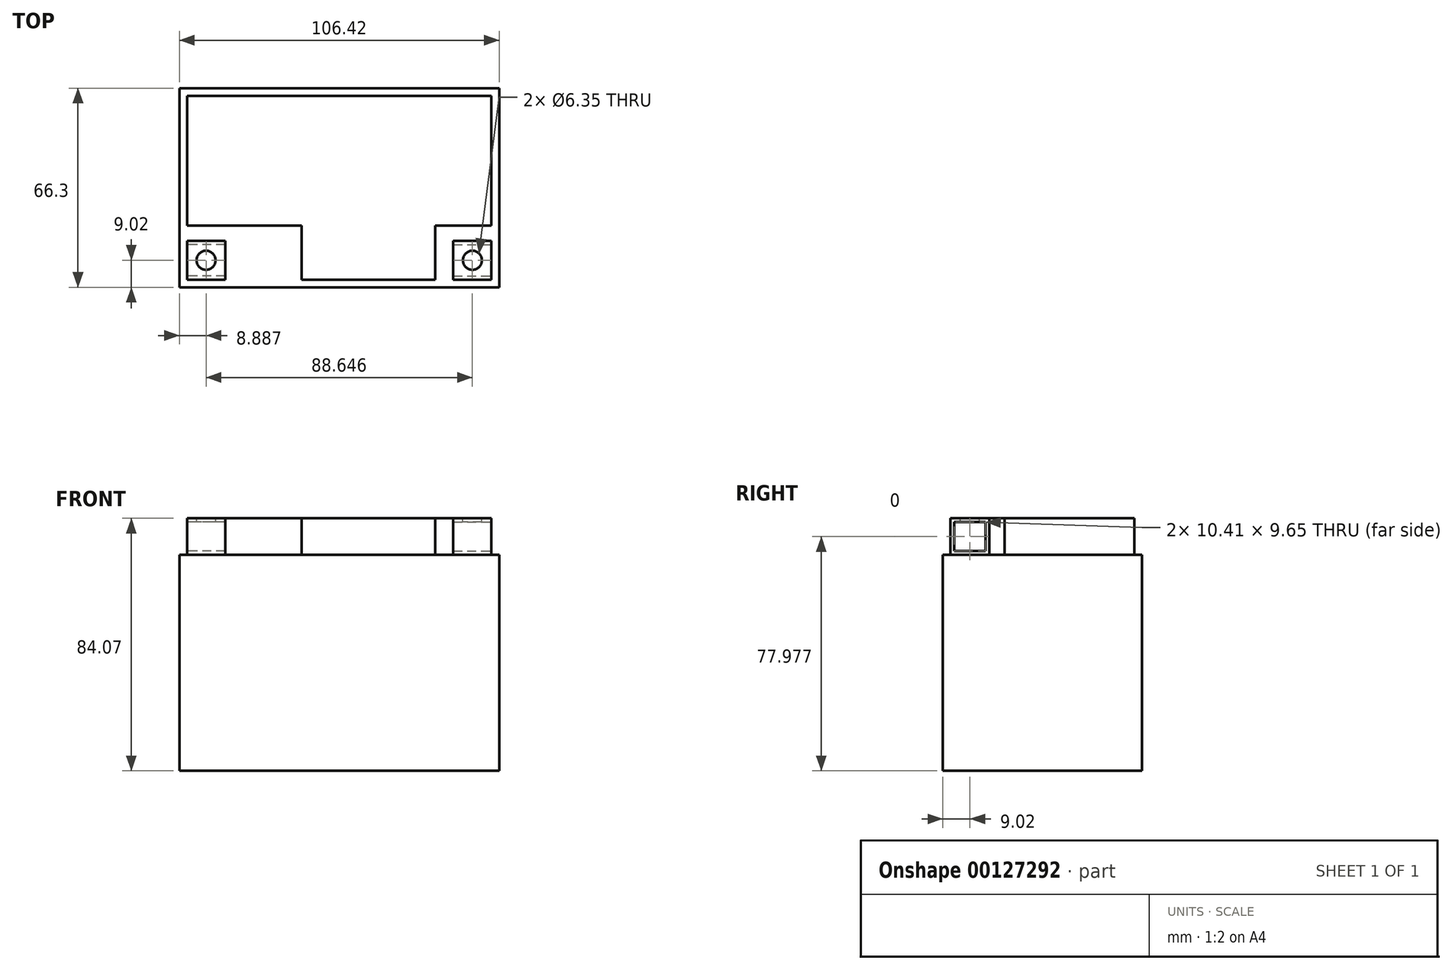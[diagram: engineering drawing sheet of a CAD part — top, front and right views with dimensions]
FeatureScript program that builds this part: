
annotation { "Feature Type Name" : "Feature", "Feature Type Description" : "" }
export const myFeature = defineFeature(function(context is Context, id is Id, definition is map)
    precondition{}
    {
        {
            var Q0;
            Q0=qCreatedBy(makeId("Top.planeOp"),FACE);
            var sketch = newSketch(context, id + "F0", { "sketchPlane" : qUnion([Q0])});
            skLineSegment(sketch, "E0.bottom", {"start": v(53.21, 33.15) * mm, "end": v(-53.21, 33.15) * mm});
            skLineSegment(sketch, "E0.top", {"start": v(53.21, -33.15) * mm, "end": v(-53.21, -33.15) * mm});
            skLineSegment(sketch, "E0.left", {"start": v(53.21, 33.15) * mm, "end": v(53.21, -33.15) * mm});
            skLineSegment(sketch, "E0.right", {"start": v(-53.21, 33.15) * mm, "end": v(-53.21, -33.15) * mm});
            skPoint(sketch, "E0.middle", {"position": v(0, 0) * mm});
            skSolve(sketch);
        }
        {
            var Q0;
            Q0 = qSketchRegion(id + "F0", true);
            extrude(context, id + "F1", {"entities" : qUnion([Q0]), "endBound" : BoundingType.SYMMETRIC, "depth" : 71.88 * mm});
        }
        {
            var Q0;
            Q0=makeQuery(id+"F1.opExtrude","CAP_FACE",FACE,{"disambiguationData":[OSD([sQuery(id+"F0.wireOp",EDGE,"E0.bottom"),sQuery(id+"F0.wireOp",EDGE,"E0.top"),sQuery(id+"F0.wireOp",EDGE,"E0.left"),sQuery(id+"F0.wireOp",EDGE,"E0.right")])],"isStart":false});
            var sketch = newSketch(context, id + "F2", { "sketchPlane" : qUnion([Q0])});
            skLineSegment(sketch, "E1.bottom", {"start": v(-50.67, 30.6) * mm, "end": v(50.67, 30.6) * mm});
            skLineSegment(sketch, "E1.left", {"start": v(-50.67, 30.6) * mm, "end": v(-50.67, -12.57) * mm});
            skLineSegment(sketch, "E1.right", {"start": v(50.67, 30.6) * mm, "end": v(50.67, -12.57) * mm});
            skLineSegment(sketch, "E2.bottom", {"start": v(-50.67, -17.65) * mm, "end": v(-37.97, -17.65) * mm});
            skLineSegment(sketch, "E2.top", {"start": v(-50.67, -30.6) * mm, "end": v(-37.97, -30.6) * mm});
            skLineSegment(sketch, "E2.left", {"start": v(-50.67, -17.65) * mm, "end": v(-50.67, -30.6) * mm});
            skLineSegment(sketch, "E2.right", {"start": v(-37.97, -17.65) * mm, "end": v(-37.97, -30.6) * mm});
            skLineSegment(sketch, "E3.bottom", {"start": v(37.97, -17.65) * mm, "end": v(50.67, -17.65) * mm});
            skLineSegment(sketch, "E3.top", {"start": v(37.97, -30.6) * mm, "end": v(50.67, -30.6) * mm});
            skLineSegment(sketch, "E3.left", {"start": v(37.97, -17.65) * mm, "end": v(37.97, -30.6) * mm});
            skLineSegment(sketch, "E3.right", {"start": v(50.67, -17.65) * mm, "end": v(50.67, -30.6) * mm});
            skLineSegment(sketch, "E4.bottom", {"start": v(-12.57, -30.6) * mm, "end": v(31.88, -30.6) * mm});
            skLineSegment(sketch, "E4.top", {"start": v(-12.57, -12.57) * mm, "end": v(-12.57, -12.57) * mm});
            skLineSegment(sketch, "E4.left", {"start": v(-12.57, -30.6) * mm, "end": v(-12.57, -12.57) * mm});
            skLineSegment(sketch, "E4.right", {"start": v(31.88, -30.6) * mm, "end": v(31.88, -12.57) * mm});
            skLineSegment(sketch, "E5", {"start": v(31.88, -12.57) * mm, "end": v(31.88, -12.57) * mm});
            skLineSegment(sketch, "E6", {"start": v(31.88, -12.57) * mm, "end": v(50.67, -12.57) * mm});
            skLineSegment(sketch, "E7", {"start": v(-50.67, -12.57) * mm, "end": v(-12.57, -12.57) * mm});
            skSolve(sketch);
        }
        {
            var Q0;
            Q0 = qSketchRegion(id + "F2", true);
            extrude(context, id + "F3", {"entities" : qUnion([Q0]), "operationType" : NewBodyOperationType.ADD, "depth" : 12.2 * mm});
        }
        {
            var Q0;
            Q0=makeQuery(id+"F3.opExtrude","SWEPT_FACE",FACE,{"disambiguationData":[OSD([sQuery(id+"F2.wireOp",EDGE,"E2.left")])]});
            var sketch = newSketch(context, id + "F4", { "sketchPlane" : qUnion([Q0])});
            skLineSegment(sketch, "E8.0", {"start": v(18.92, 37.21) * mm, "end": v(29.34, 37.21) * mm});
            skLineSegment(sketch, "E8.1", {"start": v(18.92, 46.86) * mm, "end": v(18.92, 37.21) * mm});
            skLineSegment(sketch, "E8.2", {"start": v(29.34, 46.86) * mm, "end": v(18.92, 46.86) * mm});
            skLineSegment(sketch, "E8.3", {"start": v(29.34, 37.21) * mm, "end": v(29.34, 46.86) * mm});
            skSolve(sketch);
        }
        {
            var Q0;
            Q0 = qSketchRegion(id + "F4", true);
            extrude(context, id + "F5", {"entities" : qUnion([Q0]), "operationType" : NewBodyOperationType.REMOVE, "oppositeDirection" : true, "depth" : 12.7 * mm});
        }
        {
            var Q0;
            Q0=makeQuery(id+"F3.opExtrude","SWEPT_FACE",FACE,{"disambiguationData":[OSD([sQuery(id+"F2.wireOp",EDGE,"E3.right")])]});
            var sketch = newSketch(context, id + "F6", { "sketchPlane" : qUnion([Q0])});
            skLineSegment(sketch, "E9.0", {"start": v(-29.34, 37.21) * mm, "end": v(-18.92, 37.21) * mm});
            skLineSegment(sketch, "E9.1", {"start": v(-29.34, 46.86) * mm, "end": v(-29.34, 37.21) * mm});
            skLineSegment(sketch, "E9.2", {"start": v(-18.92, 46.86) * mm, "end": v(-29.34, 46.86) * mm});
            skLineSegment(sketch, "E9.3", {"start": v(-18.92, 37.21) * mm, "end": v(-18.92, 46.86) * mm});
            skSolve(sketch);
        }
        {
            var Q0;
            Q0 = qSketchRegion(id + "F6", true);
            extrude(context, id + "F7", {"entities" : qUnion([Q0]), "operationType" : NewBodyOperationType.REMOVE, "oppositeDirection" : true, "depth" : 12.7 * mm});
        }
        {
            var Q0;
            Q0=makeQuery(id+"F3.opExtrude","CAP_FACE",FACE,{"disambiguationData":[OSD([sQuery(id+"F2.wireOp",EDGE,"E2.bottom"),sQuery(id+"F2.wireOp",EDGE,"E2.top"),sQuery(id+"F2.wireOp",EDGE,"E2.left"),sQuery(id+"F2.wireOp",EDGE,"E2.right")])],"isStart":false});
            var sketch = newSketch(context, id + "F8", { "sketchPlane" : qUnion([Q0])});
            skCircle(sketch, "E10", {"center": v(-44.32, -24.13) * mm, "radius": 3.18 * mm});
            skSolve(sketch);
        }
        {
            var Q0;
            Q0 = qSketchRegion(id + "F8", true);
            extrude(context, id + "F9", {"entities" : qUnion([Q0]), "operationType" : NewBodyOperationType.REMOVE, "oppositeDirection" : true, "depth" : 1.27 * mm});
        }
        {
            var Q0;
            Q0=makeQuery(id+"F3.opExtrude","CAP_FACE",FACE,{"disambiguationData":[OSD([sQuery(id+"F2.wireOp",EDGE,"E3.bottom"),sQuery(id+"F2.wireOp",EDGE,"E3.top"),sQuery(id+"F2.wireOp",EDGE,"E3.left"),sQuery(id+"F2.wireOp",EDGE,"E3.right")])],"isStart":false});
            var sketch = newSketch(context, id + "F10", { "sketchPlane" : qUnion([Q0])});
            skCircle(sketch, "E11", {"center": v(44.32, -24.13) * mm, "radius": 3.18 * mm});
            skSolve(sketch);
        }
        {
            var Q0;
            Q0 = qSketchRegion(id + "F10", true);
            extrude(context, id + "F11", {"entities" : qUnion([Q0]), "operationType" : NewBodyOperationType.REMOVE, "oppositeDirection" : true, "depth" : 1.27 * mm});
        }
    });
